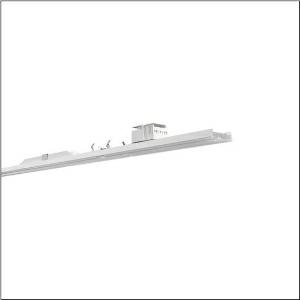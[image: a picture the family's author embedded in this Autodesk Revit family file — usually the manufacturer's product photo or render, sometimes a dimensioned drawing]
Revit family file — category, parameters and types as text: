
# Revit family: licross_r__11_recessed_mo_51tl18dv4e5f_cb05
name_source: partatom
category: Lighting Fixtures
units: mm (PartAtom-declared; Revit-internal decimal feet)

## family parameters
Cut with Voids When Loaded = No
Host = Face
Light Source = No
Part Type = Normal
Room Calculation Point = No
Round Connector Dimension = Use Diameter
Shared = No

## types (1)
- --- (1 x LED, 14980 lm, 89.5 W, 4000K)
    Apparent Load = 90 VA
    CIE Flux Codes = 83 96 99 100 100
    Color Rendering = 80
    Color Temperature = 4000K
    Default Elevation = 1800 mm
    Description = Licross® 11 Recessed MOluminaire insert, length: 2.250mm, width: 66mm, height: 67mm, LED rated luminous flux: 14.980lm, light colour: 840, control gear: DALI 2, control gear: ECG DALI, with plug, 5-pole, with phase selection, mains connection: 220..240V, AC, 50/60Hz, halogen-free wiring, primary optical cover: cover, of PMMA, light emission: direct distribution, protection rating (complete): IP40, insulation class (complete): insulation class I (protective earthing), certification: CE, ENEC, VDE, protection symbol: D if used in an environment without relevant dust loads with corresponding accessories, permissible ambient temperature for indoor applications: -25..+35°C, corresponds to IFS (International Featured Standards) requirements for safety and quality in the food industry, reducing of maximum allowable ambient temperature of 5°C with ceiling mounting, packaging unit: 1 piece
    Height = 58 mm
    Lamp = 1 x LED
    Lamp Light Flux = 14980 lm
    Lamp Power = 89.5 W
    Lamp count = 1
    Length = 2250 mm
    Luminous efficacy = 167 lm/W
    Manufacturer = Siteco
    ModVariant = No
    Model = 51TL18DV4E5F
    Mounting Place = Ceiling
    Mounting Type = Pendant
    Number of Poles = 1
    OnlyDefault = Yes
    Power Factor = 1
    Product Name = Licross® 11 Recessed MO
    Product group = luminaire insert
    ProductGroupID = 902
    Protection Class = Protection class I
    Protection Degree = IP 40
    RLX_Detail_Level = 1
    RlxData = <blob elided: 27161 chars, md5=e0402fb2>
    Socket = socket
    Standby Power = 0 W
    System Light Flux = 14980 lm
    System Power = 90 W
    Type Comments = factory setting: luminous flux: 100 % | dim-lin: 254 | 400 mA
    Type Image = l_1266722.jpg
    URL = http://relux.com
    VarID = @adj_133120
    Voltage = 0 V
    Weight = 0.00 kg
    Width = 66 mm

## geometry (parser evidence)
native form markers: Blend x4, Sweep x12
no freeform markers — native parametric forms only
